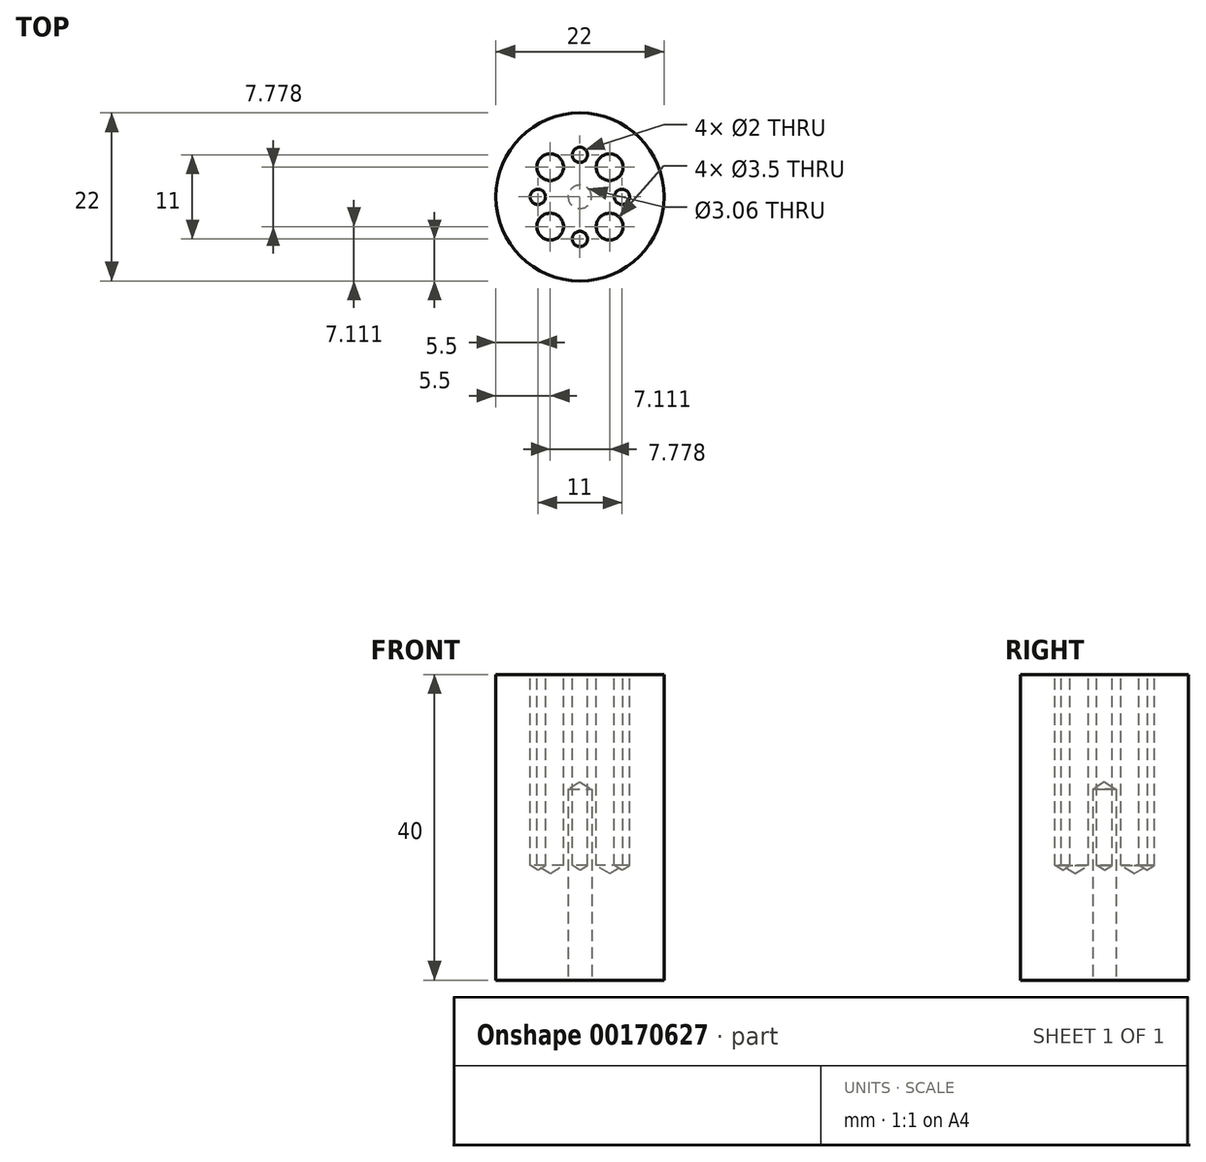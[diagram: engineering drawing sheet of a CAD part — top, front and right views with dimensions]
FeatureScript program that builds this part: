
annotation { "Feature Type Name" : "Feature", "Feature Type Description" : "" }
export const myFeature = defineFeature(function(context is Context, id is Id, definition is map)
    precondition{}
    {
        {
            var Q0;
            Q0=qCreatedBy(makeId("Top.planeOp"),FACE);
            var sketch = newSketch(context, id + "F0", { "sketchPlane" : qUnion([Q0])});
            skCircle(sketch, "E0", {"center": v(0, 0) * mm, "radius": 11 * mm});
            skSolve(sketch);
        }
        {
            var Q0;
            Q0 = qSketchRegion(id + "F0", true);
            extrude(context, id + "F1", {"entities" : qUnion([Q0]), "depth" : 40 * mm});
        }
        {
            var Q0;
            Q0=makeQuery(id+"F1.opExtrude","CAP_FACE",FACE,{"disambiguationData":[OSD([sQuery(id+"F0.wireOp",EDGE,"E0")])],"isStart":true});
            var sketch = newSketch(context, id + "F2", { "sketchPlane" : qUnion([Q0])});
            skPoint(sketch, "E1", {"position": v(0, 0) * mm});
            skSolve(sketch);
        }
        {
            var Q0;
            Q0=sQuery(id+"F2.wireOp",VERTEX,"E1");
            var Q1;
            Q1=makeQuery(id+"F1.opExtrude","SWEPT_BODY",BODY,{"disambiguationData":[OSD([sQuery(id+"F0.wireOp",EDGE,"E0")])]});
            hole(context, id + "F3", {"style" : HoleStyle.SIMPLE, "endStyle" : HoleEndStyle.BLIND, "holeDiameter" : 3.06 * mm, "holeDepth" : 25 * mm, "locations" : qUnion([Q0]), "scope" : qUnion([Q1])});
        }
        {
            var Q0;
            Q0=makeQuery(id+"F1.opExtrude","CAP_FACE",FACE,{"disambiguationData":[OSD([sQuery(id+"F0.wireOp",EDGE,"E0")])],"isStart":false});
            var sketch = newSketch(context, id + "F4", { "sketchPlane" : qUnion([Q0])});
            skPoint(sketch, "E2", {"position": v(0, 5.5) * mm});
            skPoint(sketch, "E3", {"position": v(5.5, 0) * mm});
            skPoint(sketch, "E4", {"position": v(0, -5.5) * mm});
            skPoint(sketch, "E5", {"position": v(-5.5, 0) * mm});
            skSolve(sketch);
        }
        {
            var Q0;
            Q0=sQuery(id+"F4.wireOp",VERTEX,"E2");
            var Q1;
            Q1=sQuery(id+"F4.wireOp",VERTEX,"E3");
            var Q2;
            Q2=sQuery(id+"F4.wireOp",VERTEX,"E5");
            var Q3;
            Q3=sQuery(id+"F4.wireOp",VERTEX,"E4");
            var Q4;
            Q4=makeQuery(id+"F1.opExtrude","SWEPT_BODY",BODY,{"disambiguationData":[OSD([sQuery(id+"F0.wireOp",EDGE,"E0")])]});
            hole(context, id + "F5", {"style" : HoleStyle.SIMPLE, "endStyle" : HoleEndStyle.BLIND, "holeDiameter" : 2 * mm, "holeDepth" : 25 * mm, "locations" : qUnion([Q0, Q1, Q2, Q3]), "scope" : qUnion([Q4])});
        }
        {
            var Q0;
            Q0=makeQuery(id+"F1.opExtrude","CAP_FACE",FACE,{"disambiguationData":[OSD([sQuery(id+"F0.wireOp",EDGE,"E0")])],"isStart":false});
            var sketch = newSketch(context, id + "F6", { "sketchPlane" : qUnion([Q0])});
            skLineSegment(sketch, "E6", {"start": v(-9.7, 9.7) * mm, "end": v(9.13, -9.13) * mm, "construction": true});
            skLineSegment(sketch, "E7", {"start": v(10.15, 10.15) * mm, "end": v(-8.78, -8.78) * mm, "construction": true});
            skPoint(sketch, "E8", {"position": v(3.89, 3.89) * mm});
            skPoint(sketch, "E9", {"position": v(-3.89, 3.89) * mm});
            skPoint(sketch, "E10", {"position": v(-3.89, -3.89) * mm});
            skPoint(sketch, "E11", {"position": v(3.89, -3.89) * mm});
            skSolve(sketch);
        }
        {
            var Q0;
            Q0=sQuery(id+"F6.wireOp",VERTEX,"E9");
            var Q1;
            Q1=sQuery(id+"F6.wireOp",VERTEX,"E8");
            var Q2;
            Q2=sQuery(id+"F6.wireOp",VERTEX,"E11");
            var Q3;
            Q3=sQuery(id+"F6.wireOp",VERTEX,"E10");
            var Q4;
            Q4=makeQuery(id+"F1.opExtrude","SWEPT_BODY",BODY,{"disambiguationData":[OSD([sQuery(id+"F0.wireOp",EDGE,"E0")])]});
            hole(context, id + "F7", {"style" : HoleStyle.SIMPLE, "endStyle" : HoleEndStyle.BLIND, "holeDiameter" : 3.5 * mm, "holeDepth" : 25 * mm, "locations" : qUnion([Q0, Q1, Q2, Q3]), "scope" : qUnion([Q4])});
        }
    });
